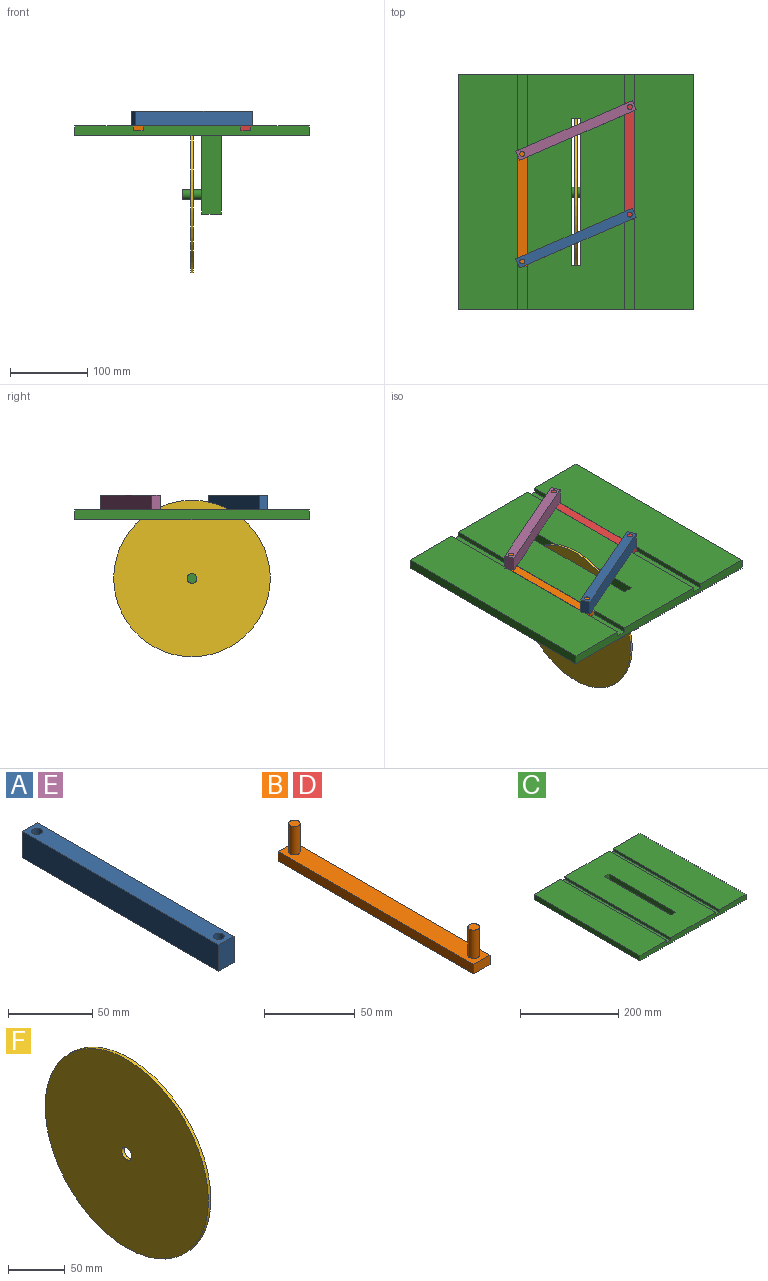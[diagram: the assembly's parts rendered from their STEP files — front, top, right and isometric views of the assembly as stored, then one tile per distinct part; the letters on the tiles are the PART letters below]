
ASSEMBLY  parts=6 mates=7
PART A: 8 faces, bbox 12.7x165.1x19.1 mm
  f0: plane 19.05x12.7mm, normal (0,1,0), area 241.9mm2, adj f1,f4,f6,f7
  f1: plane 165.1x19.05mm, normal (-1,0,0), area 3145.2mm2, adj f0,f2,f6,f7
  f2: plane 19.05x12.7mm, normal (0,-1,0), area 241.9mm2, adj f1,f4,f6,f7
  f3: cylinder r=3.17mm len=19.05mm, axis (0,0,-1), area 380mm2, adj f6,f7
  f4: plane 165.1x19.05mm, normal (1,0,0), area 3145.2mm2, adj f0,f2,f6,f7
  f5: cylinder r=3.17mm len=19.05mm, axis (0,0,-1), area 380mm2, adj f6,f7
  f6: plane 165.1x12.7mm, normal (0,0,1), area 2033.4mm2, adj f0,f1,f2,f3,f4,f5
  f7: plane 165.1x12.7mm, normal (0,0,-1), area 2033.4mm2, adj f0,f1,f2,f3,f4,f5
PART B: 10 faces, bbox 12.7x152.4x25.4 mm
  f0: plane 152.4x6.35mm, normal (1,0,0), area 967.7mm2, adj f1,f3,f4,f5
  f1: plane 12.7x6.35mm, normal (0,1,0), area 80.6mm2, adj f0,f2,f4,f5
  f2: plane 152.4x6.35mm, normal (-1,0,0), area 967.7mm2, adj f1,f3,f4,f5
  f3: plane 12.7x6.35mm, normal (0,-1,0), area 80.6mm2, adj f0,f2,f4,f5
  f4: plane 152.4x12.7mm, normal (0,0,1), area 1872.1mm2, adj f0,f1,f2,f3,f6,f8
  f5: plane 152.4x12.7mm, normal (0,0,-1), area 1935.5mm2, adj f0,f1,f2,f3
  f6: cylinder r=3.17mm len=19.05mm, axis (0,0,-1), area 380mm2, adj f4,f7
  f7: plane 6.35x6.35mm, normal (0,0,1), area 31.7mm2, adj f6
  f8: cylinder r=3.17mm len=19.05mm, axis (0,0,-1), area 380mm2, adj f4,f9
  f9: plane 6.35x6.35mm, normal (0,0,1), area 31.7mm2, adj f8
PART C: 25 faces, bbox 304.8x304.8x114.3 mm
  f0: plane 304.8x304.8mm, normal (0,0,-1), area 89193.4mm2, adj f3,f4,f5,f6,f7,f8,f9,f10
  f1: plane 304.8x12.7mm, normal (0,0,1), area 3871mm2, adj f7,f9,f12,f14
  f2: plane 304.8x12.7mm, normal (0,0,1), area 3871mm2, adj f7,f9,f11,f16
  f3: plane 190.5x12.7mm, normal (-1,0,0), area 2419.3mm2, adj f0,f4,f10,f13
  f4: plane 12.7x12.7mm, normal (0,1,0), area 161.3mm2, adj f0,f3,f5,f13
  f5: plane 190.5x12.7mm, normal (1,0,0), area 2419.3mm2, adj f0,f4,f10,f13
  f6: plane 304.8x12.7mm, normal (1,0,0), area 3871mm2, adj f0,f7,f9,f17
  f7: plane 304.8x12.7mm, normal (0,1,0), area 3709.7mm2, adj f0,f1,f2,f6,f8,f11,f12,f13
  f8: plane 304.8x12.7mm, normal (-1,0,0), area 3871mm2, adj f0,f7,f9,f15
  f9: plane 304.8x12.7mm, normal (0,-1,0), area 3709.7mm2, adj f0,f1,f2,f6,f8,f11,f12,f13
  f10: plane 12.7x12.7mm, normal (0,-1,0), area 161.3mm2, adj f0,f3,f5,f13
  f11: plane 304.8x6.35mm, normal (1,0,0), area 1935.5mm2, adj f2,f7,f9,f13
  f12: plane 304.8x6.35mm, normal (-1,0,0), area 1935.5mm2, adj f1,f7,f9,f13
  f13: plane 304.8x127mm, normal (0,0,1), area 36290.3mm2, adj f3,f4,f5,f7,f9,f10,f11,f12
  f14: plane 304.8x6.35mm, normal (1,0,0), area 1935.5mm2, adj f1,f7,f9,f15
  f15: plane 304.8x76.2mm, normal (0,0,1), area 23225.8mm2, adj f7,f8,f9,f14
  f16: plane 304.8x6.35mm, normal (-1,0,0), area 1935.5mm2, adj f2,f7,f9,f17
  f17: plane 304.8x76.2mm, normal (0,0,1), area 23225.8mm2, adj f6,f7,f9,f16
  f18: plane 101.6x50.8mm, normal (-1,0,0), area 5161.3mm2, adj f0,f19,f21,f22
  f19: plane 101.6x25.4mm, normal (0,-1,0), area 2580.6mm2, adj f0,f18,f20,f22
  f20: plane 101.6x50.8mm, normal (1,0,0), area 5034.6mm2, adj f0,f19,f21,f22,f23
  f21: plane 101.6x25.4mm, normal (0,1,0), area 2580.6mm2, adj f0,f18,f20,f22
  f22: plane 50.8x25.4mm, normal (0,0,-1), area 1290.3mm2, adj f18,f19,f20,f21
  f23: cylinder r=6.35mm len=25.4mm, axis (-1,0,0), area 1013.4mm2, adj f20,f24
  f24: plane 12.7x12.7mm, normal (1,0,0), area 126.7mm2, adj f23
PART D: same geometry as B
PART E: same geometry as A
PART F: 4 faces, bbox 3.2x203.2x203.2 mm
  f0: cylinder r=6.35mm len=12.7mm, axis (-1,0,0), area 126.7mm2, adj f2,f3
  f1: cylinder r=101.6mm len=203.2mm, axis (-1,0,0), area 2026.8mm2, adj f2,f3
  f2: plane 203.2x203.2mm, normal (1,0,0), area 32302.6mm2, adj f0,f1
  f3: plane 203.2x203.2mm, normal (-1,0,0), area 32302.6mm2, adj f0,f1
PLACE A rot(axis=(0,0,-1),66.4deg) t=(112.37,49.92,-7.33)mm
PLACE B rot(axis=(0,0,-1),180deg) t=(42.52,89.31,-13.68)mm
PLACE C rot(axis=(0,0,1),180deg) t=(112.37,109.76,-20.03)mm
PLACE D rot(axis=(0.11,-0.04,0.99),0deg) t=(182.22,150.22,-13.68)mm
PLACE E rot(axis=(0,0,-1),66.4deg) t=(112.37,189.62,-7.33)mm
PLACE F t=(110.78,109.76,-96.23)mm
MATE revolute A.f3 <-> D.f6  axis (0,0,-1) through (182.22,80.37,2.19)mm
MATE revolute D.f8 <-> E.f3  axis (0,0,-1) through (182.22,220.07,2.19)mm
MATE planar D.f5 <-> C.f1  axis (0,0,-1) through (182.22,150.22,-13.68)mm
MATE revolute F.f0 <-> C.f23  axis (-1,0,0) through (112.37,109.76,-96.23)mm
MATE revolute A.f5 <-> B.f8  axis (0,0,-1) through (42.52,19.46,2.19)mm
MATE planar B.f5 <-> C.f2  axis (0,0,-1) through (42.52,89.31,-13.68)mm
MATE revolute E.f5 <-> B.f6  axis (0,0,-1) through (42.52,159.16,2.19)mm
